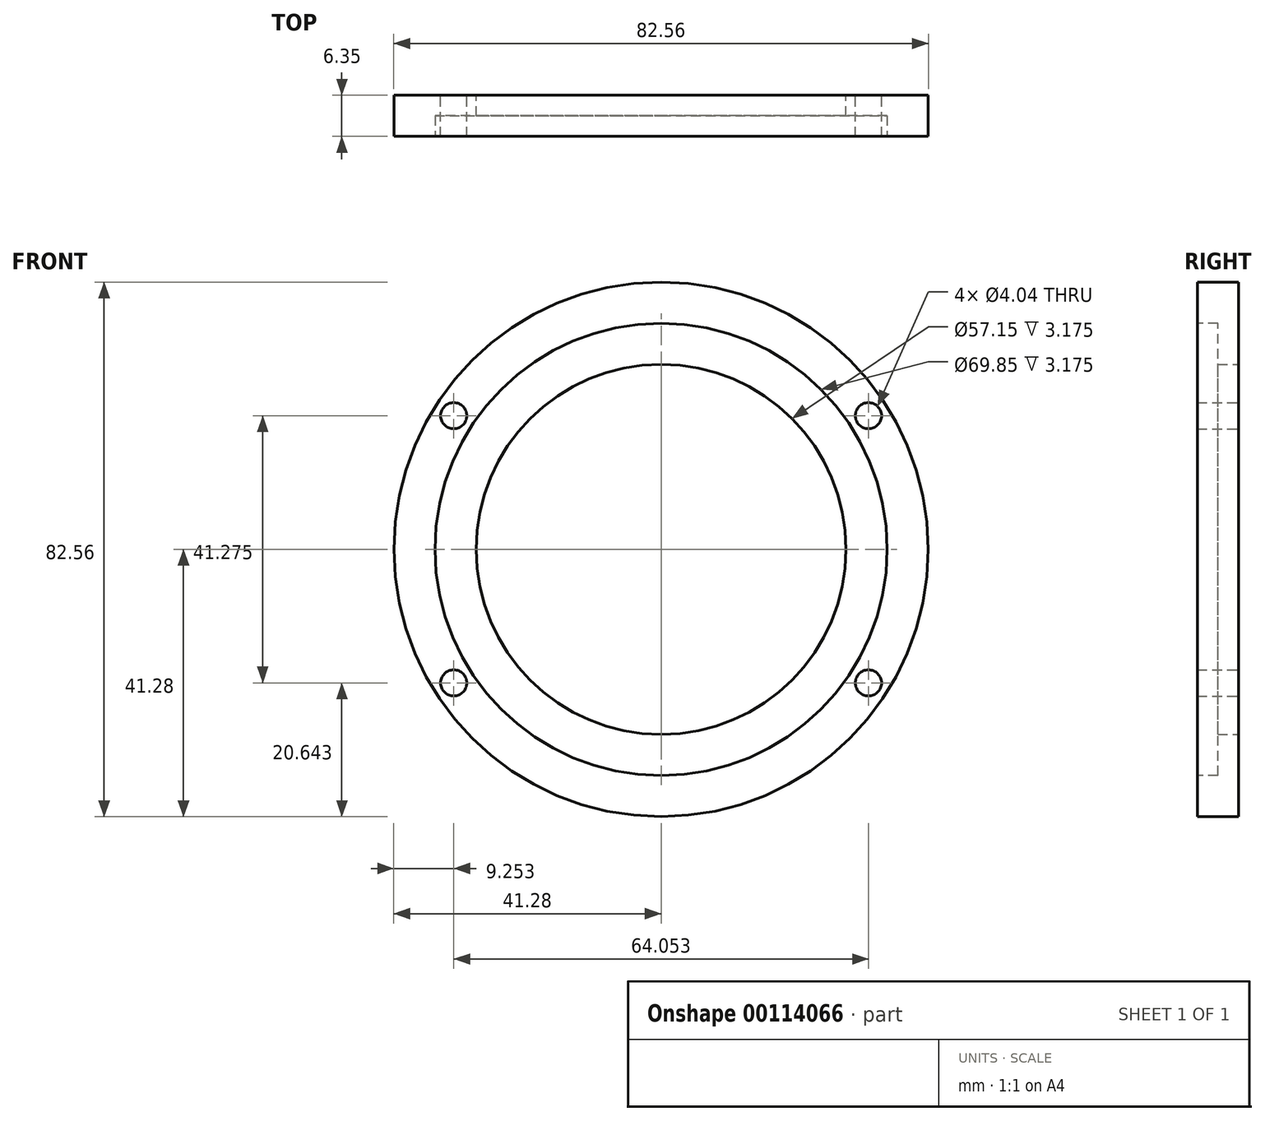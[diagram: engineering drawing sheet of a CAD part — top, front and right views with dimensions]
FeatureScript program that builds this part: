
annotation { "Feature Type Name" : "Feature", "Feature Type Description" : "" }
export const myFeature = defineFeature(function(context is Context, id is Id, definition is map)
    precondition{}
    {
        {
            var Q0;
            Q0=qCreatedBy(makeId("Front.planeOp"),FACE);
            var sketch = newSketch(context, id + "F0", { "sketchPlane" : qUnion([Q0])});
            skCircle(sketch, "E0", {"center": v(0, 0) * mm, "radius": 41.28 * mm});
            skCircle(sketch, "E1", {"center": v(0, 0) * mm, "radius": 28.58 * mm});
            skSolve(sketch);
        }
        {
            var Q0;
            Q0 = qSketchRegion(id + "F0", true);
            extrude(context, id + "F1", {"entities" : qUnion([Q0]), "depth" : 6.35 * mm});
        }
        {
            var Q0;
            Q0=makeQuery(id+"F1.opExtrude","CAP_FACE",FACE,{"disambiguationData":[OSD([sQuery(id+"F0.wireOp",EDGE,"E0"),sQuery(id+"F0.wireOp",EDGE,"E1")])],"isStart":false});
            var sketch = newSketch(context, id + "F2", { "sketchPlane" : qUnion([Q0])});
            skCircle(sketch, "E2", {"center": v(0, 0) * mm, "radius": 34.93 * mm});
            skSolve(sketch);
        }
        {
            var Q0;
            Q0 = qSketchRegion(id + "F2", true);
            extrude(context, id + "F3", {"entities" : qUnion([Q0]), "operationType" : NewBodyOperationType.REMOVE, "oppositeDirection" : true, "depth" : 3.17 * mm});
        }
        {
            var Q0;
            Q0=makeQuery(id+"F1.opExtrude","CAP_FACE",FACE,{"disambiguationData":[OSD([sQuery(id+"F0.wireOp",EDGE,"E0"),sQuery(id+"F0.wireOp",EDGE,"E1")])],"isStart":false});
            var sketch = newSketch(context, id + "F4", { "sketchPlane" : qUnion([Q0])});
            skPoint(sketch, "E3", {"position": v(-63.44, 35.32) * mm});
            skLineSegment(sketch, "E4", {"start": v(-32.03, 0) * mm, "end": v(-32.03, 20.64) * mm, "construction": true});
            skLineSegment(sketch, "E5", {"start": v(-32.03, 20.64) * mm, "end": v(0, 20.64) * mm, "construction": true});
            skLineSegment(sketch, "E6", {"start": v(-49.1, 0) * mm, "end": v(-19.94, 45.26) * mm, "construction": true});
            skLineSegment(sketch, "E7", {"start": v(-34.7, 22.36) * mm, "end": v(-29.36, 18.92) * mm, "construction": true});
            skPoint(sketch, "E8", {"position": v(-32.03, 20.64) * mm});
            skPoint(sketch, "E9.MirrorP", {"position": v(32.03, 20.64) * mm});
            skPoint(sketch, "E10.MirrorP", {"position": v(-32.03, -20.64) * mm});
            skPoint(sketch, "E11.MirrorP", {"position": v(32.03, -20.64) * mm});
            skSolve(sketch);
        }
        {
            var Q0;
            Q0=sQuery(id+"F4.wireOp",VERTEX,"E8");
            var Q1;
            Q1=sQuery(id+"F4.wireOp",VERTEX,"E9.MirrorP");
            var Q2;
            Q2=sQuery(id+"F4.wireOp",VERTEX,"E11.MirrorP");
            var Q3;
            Q3=sQuery(id+"F4.wireOp",VERTEX,"E10.MirrorP");
            var Q4;
            Q4=makeQuery(id+"F1.opExtrude","SWEPT_BODY",BODY,{"disambiguationData":[OSD([sQuery(id+"F0.wireOp",EDGE,"E0"),sQuery(id+"F0.wireOp",EDGE,"E1")])]});
            hole(context, id + "F5", {"style" : HoleStyle.SIMPLE, "endStyle" : HoleEndStyle.BLIND, "standardTappedOrClearance" : lookupTablePath({ "standard" : "ANSI", "engagement" : "75%", "pitch" : "32 tpi", "size" : "#10", "type" : "Tapped" }), "standardBlindInLast" : lookupTablePath({ "standard" : "ANSI", "engagement" : "75%", "pitch" : "32 tpi", "size" : "#10", "type" : "Tapped" }), "holeDiameter" : 4.04 * mm, "holeDepth" : 6.35 * mm, "locations" : qUnion([Q0, Q1, Q2, Q3]), "scope" : qUnion([Q4]), "majorDiameter" : 4.83 * mm});
        }
    });
